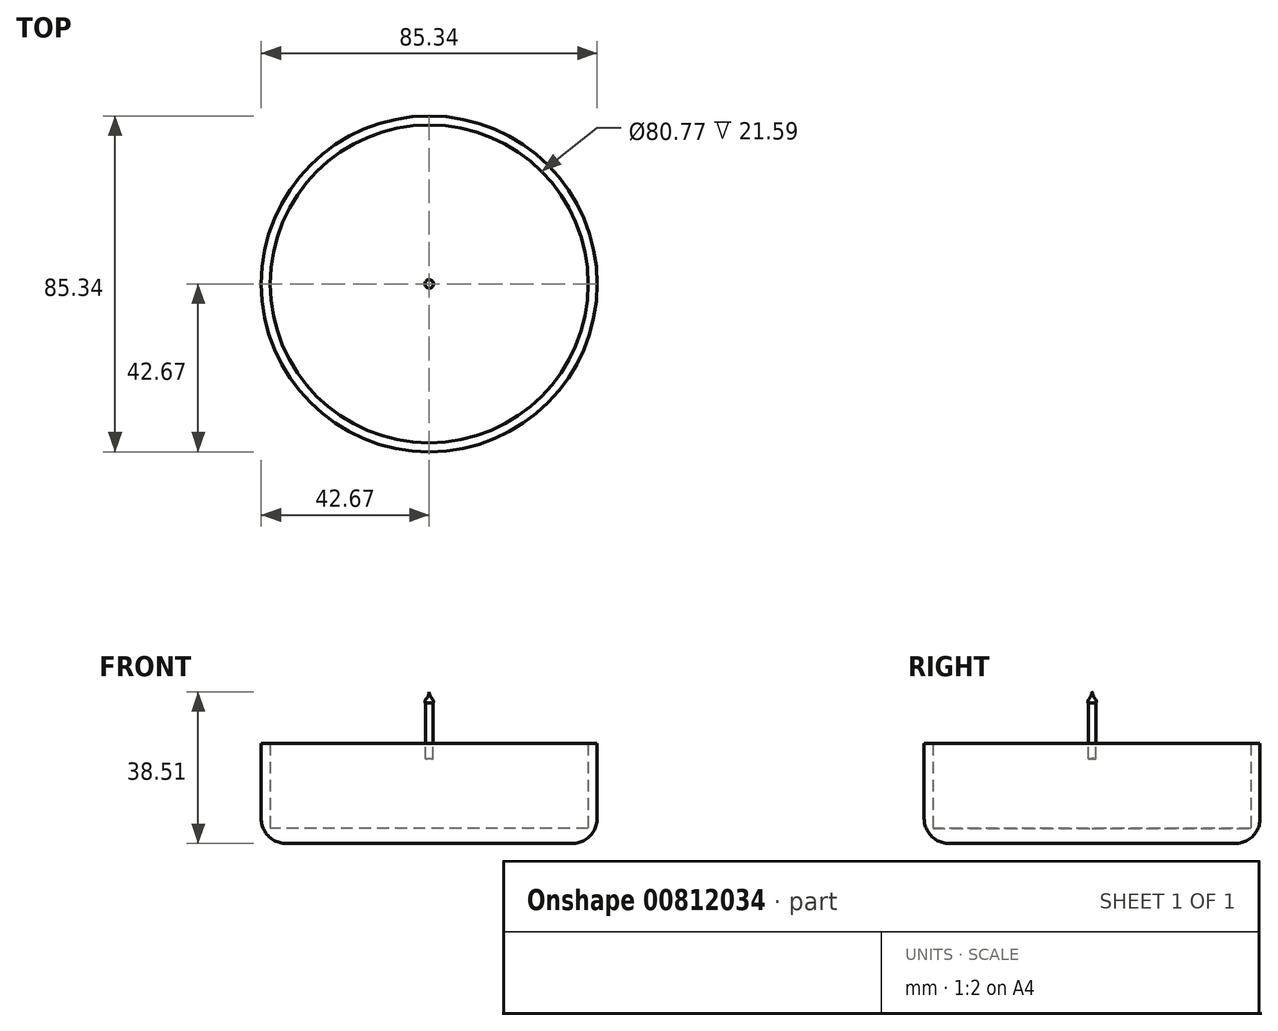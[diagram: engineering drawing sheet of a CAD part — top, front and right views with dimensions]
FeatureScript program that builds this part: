
annotation { "Feature Type Name" : "Feature", "Feature Type Description" : "" }
export const myFeature = defineFeature(function(context is Context, id is Id, definition is map)
    precondition{}
    {
        {
            var Q0;
            Q0=qCreatedBy(makeId("Top.planeOp"),FACE);
            var sketch = newSketch(context, id + "F0", { "sketchPlane" : qUnion([Q0])});
            skCircle(sketch, "E0", {"center": v(0, 0) * mm, "radius": 42.67 * mm});
            skCircle(sketch, "E1", {"center": v(0, 0) * mm, "radius": 40.39 * mm});
            skSolve(sketch);
        }
        {
            var Q0;
            Q0=qCreatedBy(makeId("Front.planeOp"),FACE);
            var sketch = newSketch(context, id + "F1", { "sketchPlane" : qUnion([Q0])});
            skLineSegment(sketch, "E2.bottom", {"start": v(-0.4, 0) * mm, "end": v(0.35, 0) * mm});
            skPoint(sketch, "E3.1.internal.snap0", {"position": v(-0.03, 29.03) * mm});
            skLineSegment(sketch, "E4", {"start": v(0, 35.66) * mm, "end": v(0, 0) * mm});
            skLineSegment(sketch, "E5", {"start": v(0, 0) * mm, "end": v(-22.66, 0) * mm});
            skFitSpline(sketch, "E6", {"points": [v(-22.66, 0) * mm, v(-0.4, 21.57) * mm, v(25.48, 2.8) * mm], "startDerivative": vector(43.26, 63.51) * mm, "endDerivative": vector(53, -57.61) * mm});
            skLineSegment(sketch, "E7", {"start": v(0, 35.66) * mm, "end": v(0, 38.5) * mm});
            skLineSegment(sketch, "E8", {"start": v(0, 35.66) * mm, "end": v(-0.96, 35.66) * mm});
            skFitSpline(sketch, "E9", {"points": [v(0, 38.5) * mm, v(-0.96, 35.66) * mm], "startDerivative": vector(0, -4.27) * mm, "endDerivative": vector(1.68, -2.49) * mm});
            skLineSegment(sketch, "E10", {"start": v(-0.96, 35.66) * mm, "end": v(-0.96, 21.52) * mm});
            skSolve(sketch);
        }
        {
            var Q0;
            Q0=makeQuery(id+"F0.imprint","IMPRINT",FACE,{"disambiguationData":[TD([[makeQuery(id+"F0.imprint","IMPRINT",EDGE,{"derivedFrom":sQuery(id+"F0.wireOp",EDGE,"E0")}),1.0]])]});
            extrude(context, id + "F2", {"entities" : qUnion([Q0]), "depth" : 25.4 * mm, "offsetDistance" : 25.4 * mm});
        }
        {
            var Q0;
            Q0=makeQuery(id+"F0.imprint","IMPRINT",FACE,{"disambiguationData":[TD([[makeQuery(id+"F0.imprint","IMPRINT",EDGE,{"derivedFrom":sQuery(id+"F0.wireOp",EDGE,"E1")}),1.0]])]});
            extrude(context, id + "F3", {"entities" : qUnion([Q0]), "operationType" : NewBodyOperationType.ADD, "depth" : 3.8 * mm, "offsetDistance" : 25.4 * mm});
        }
        {
            var Q0;
            {var subQ0=sQuery(id+"F1.wireOp",EDGE,"E5");var subQ1=sQuery(id+"F1.wireOp",EDGE,"E4");var subQ2=makeQuery(id+"F1.imprint","INTERSECT",VERTEX,{"derivedFrom":[subQ1,subQ0]});Q0=makeQuery(id+"F1.imprint","IMPRINT",FACE,{"disambiguationData":[TD([[makeQuery(id+"F1.imprint","IMPRINT",EDGE,{"disambiguationData":[TD([[subQ2,1.0]])],"derivedFrom":subQ1}),-1.0]])]});}
            var Q1;
            {var subQ0=sQuery(id+"F1.wireOp",EDGE,"cgpnvOUZ-5iWF-ww9u-AtpI-tp9S1ovTieda");Q1=makeQuery(id+"F1.imprint","IMPRINT",FACE,{"disambiguationData":[TD([[makeQuery(id+"F1.imprint","IMPRINT",EDGE,{"derivedFrom":subQ0}),1.0]])]});}
            var Q2;
            Q2=makeQuery(id+"F1.imprint","IMPRINT",FACE,{"disambiguationData":[TD([[makeQuery(id+"F1.imprint","IMPRINT",EDGE,{"derivedFrom":sQuery(id+"F1.wireOp",EDGE,"E7")}),1.0]])]});
            var Q3;
            {var subQ0=sQuery(id+"F1.wireOp",EDGE,"E8");Q3=makeQuery(id+"F1.imprint","IMPRINT",FACE,{"disambiguationData":[TD([[makeQuery(id+"F1.imprint","IMPRINT",EDGE,{"derivedFrom":subQ0}),1.0]])]});}
            var Q4;
            Q4=sQuery(id+"F1.wireOp",EDGE,"E4");
            revolve(context, id + "F4", {"operationType" : NewBodyOperationType.ADD, "surfaceOperationType" : NewSurfaceOperationType.NEW, "entities" : qUnion([Q0, Q1, Q2, Q3]), "axis" : qUnion([Q4]), "revolveType" : RevolveType.FULL});
        }
        {
            var Q0;
            Q0=makeQuery(id+"F3.opExtrude","CAP_EDGE",EDGE,{"disambiguationData":[OSD([sQuery(id+"F0.wireOp",EDGE,"E1")])],"isStart":false});
            var Q1;
            Q1=makeQuery(id+"F2.opExtrude","CAP_EDGE",EDGE,{"disambiguationData":[OSD([sQuery(id+"F0.wireOp",EDGE,"E0")])],"isStart":true});
            fillet(context, id + "F5", {"entities" : qUnion([Q0, Q1]), "radius" : 6.35 * mm, "tangentPropagation" : true, "allowEdgeOverflow" : false});
        }
    });
